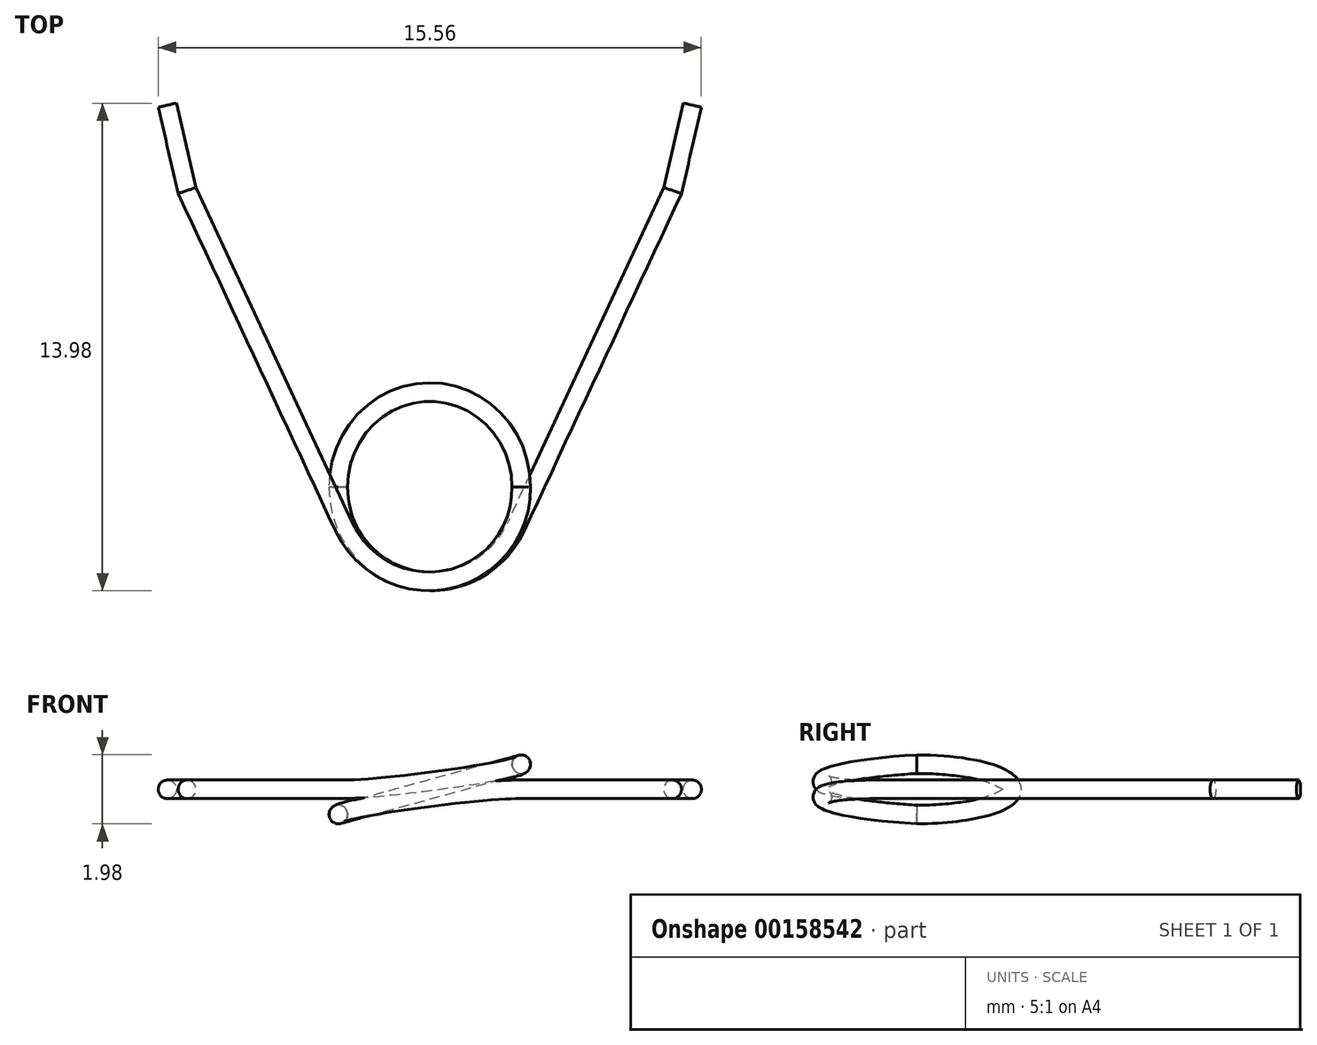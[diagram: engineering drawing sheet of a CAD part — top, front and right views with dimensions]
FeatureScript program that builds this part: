
annotation { "Feature Type Name" : "Feature", "Feature Type Description" : "" }
export const myFeature = defineFeature(function(context is Context, id is Id, definition is map)
    precondition{}
    {
        {
            var Q0;
            Q0=qCreatedBy(makeId("Top.planeOp"),FACE);
            var sketch = newSketch(context, id + "F0", { "sketchPlane" : qUnion([Q0])});
            skCircle(sketch, "E0", {"center": v(0, 0) * mm, "radius": 2.98 * mm, "construction": true});
            skLineSegment(sketch, "E1", {"start": v(2.7, -1.26) * mm, "end": v(7.21, 8.4) * mm});
            skLineSegment(sketch, "E2", {"start": v(7.21, 8.4) * mm, "end": v(7.78, 10.88) * mm});
            skLineSegment(sketch, "E3", {"start": v(-16.33, -2.98) * mm, "end": v(8.7, -2.98) * mm, "construction": true});
            skLineSegment(sketch, "E4", {"start": v(0, 0) * mm, "end": v(0, 10.51) * mm, "construction": true});
            skLineSegment(sketch, "E5", {"start": v(-2.7, -1.26) * mm, "end": v(-7.21, 8.4) * mm, "construction": true});
            skLineSegment(sketch, "E6", {"start": v(-7.21, 8.4) * mm, "end": v(-7.78, 10.88) * mm, "construction": true});
            skSolve(sketch);
        }
        {
            var Q0;
            Q0=sQuery(id+"F0.wireOp",EDGE,"E2");
            var Q1;
            Q1=sQuery(id+"F0.wireOp",VERTEX,"E2.end");
            cPlane(context, id + "F1", {"entities" : qUnion([Q0, Q1]), "cplaneType" : CPlaneType.LINE_POINT, "offset" : 25.4 * mm, "width" : 152.4 * mm, "height" : 152.4 * mm});
        }
        {
            var Q0;
            Q0=qCreatedBy(id+"F1.planeOp",FACE);
            var sketch = newSketch(context, id + "F2", { "sketchPlane" : qUnion([Q0])});
            skCircle(sketch, "E7", {"center": v(-4.87, 0) * mm, "radius": 0.27 * mm});
            skSolve(sketch);
        }
        {
            var Q0;
            Q0=makeQuery(id+"F2.imprint","IMPRINT",FACE,{"disambiguationData":[TD([[makeQuery(id+"F2.imprint","IMPRINT",EDGE,{"derivedFrom":sQuery(id+"F2.wireOp",EDGE,"E7")}),1.0]])]});
            var Q1;
            Q1=sQuery(id+"F0.wireOp",EDGE,"E2");
            var Q2;
            Q2=sQuery(id+"F0.wireOp",EDGE,"E1");
            sweep(context, id + "F3", {"profiles" : qUnion([Q0]), "path" : qUnion([Q1, Q2])});
        }
        {
            var Q0;
            Q0=makeQuery(id+"F3.opSweep","CAP_FACE",FACE,{"disambiguationData":[OSD([sQuery(id+"F0.wireOp",VERTEX,"E1.start"),sQuery(id+"F2.wireOp",EDGE,"E7")])],"isStart":false});
            var sketch = newSketch(context, id + "F4", { "sketchPlane" : qUnion([Q0])});
            skLineSegment(sketch, "E8", {"start": v(0, 0) * mm, "end": v(0.05, -0.38) * mm, "construction": true});
            skLineSegment(sketch, "E9", {"start": v(0.05, -0.38) * mm, "end": v(2.72, 0) * mm, "construction": true});
            skCircle(sketch, "E10.0", {"center": v(2.72, 0) * mm, "radius": 0.27 * mm});
            skSolve(sketch);
        }
        {
            var Q0;
            Q0 = qSketchRegion(id + "F4", true);
            var Q1;
            Q1=sQuery(id+"F4.wireOp",EDGE,"E8");
            revolve(context, id + "F5", {"operationType" : NewBodyOperationType.ADD, "entities" : qUnion([Q0]), "axis" : qUnion([Q1]), "revolveType" : RevolveType.ONE_DIRECTION, "angle" : 270 * degree});
        }
        {
            var Q0;
            Q0=qCreatedBy(makeId("Top.planeOp"),FACE);
            var sketch = newSketch(context, id + "F6", { "sketchPlane" : qUnion([Q0])});
            skLineSegment(sketch, "E11.bottom", {"start": v(-4.83, 4.58) * mm, "end": v(1.68, 4.58) * mm});
            skLineSegment(sketch, "E11.top", {"start": v(-4.83, 0) * mm, "end": v(1.68, 0) * mm});
            skLineSegment(sketch, "E11.left", {"start": v(-4.83, 4.58) * mm, "end": v(-4.83, 0) * mm});
            skLineSegment(sketch, "E11.right", {"start": v(1.68, 4.58) * mm, "end": v(1.68, 0) * mm});
            skSolve(sketch);
        }
        {
            var Q0;
            Q0 = qSketchRegion(id + "F6", true);
            extrude(context, id + "F7", {"entities" : qUnion([Q0]), "operationType" : NewBodyOperationType.REMOVE, "oppositeDirection" : true, "depth" : 25.4 * mm});
        }
        {
            var Q0;
            Q0=makeQuery(id+"F7.boolean.opBoolean","COPY",FACE,{"derivedFrom":makeQuery(id+"F7.opExtrude","SWEPT_FACE",FACE,{"disambiguationData":[OSD([sQuery(id+"F6.wireOp",EDGE,"E11.top")])]})});
            var sketch = newSketch(context, id + "F8", { "sketchPlane" : qUnion([Q0])});
            skLineSegment(sketch, "E12", {"start": v(0, 0) * mm, "end": v(2.62, -0.72) * mm, "construction": true});
            skLineSegment(sketch, "E13", {"start": v(0, 0) * mm, "end": v(0.13, 0.48) * mm, "construction": true});
            skCircle(sketch, "E14", {"center": v(2.62, -0.72) * mm, "radius": 0.27 * mm});
            skSolve(sketch);
        }
        {
            var Q0;
            Q0=makeQuery(id+"F3.opSweep","SWEPT_BODY",BODY,{"disambiguationData":[OSD([sQuery(id+"F0.wireOp",EDGE,"E1"),sQuery(id+"F2.wireOp",EDGE,"E7")])]});
            var Q1;
            Q1=sQuery(id+"F0.wireOp",EDGE,"E4");
            circularPattern(context, id + "F9", {"entities" : qUnion([Q0]), "axis" : qUnion([Q1]), "angle" : 180 * degree, "instanceCount" : 2});
        }
        {
            var Q0;
            Q0 = qSketchRegion(id + "F8", true);
            var Q1;
            Q1=sQuery(id+"F8.wireOp",EDGE,"E13");
            revolve(context, id + "F10", {"entities" : qUnion([Q0]), "axis" : qUnion([Q1]), "revolveType" : RevolveType.ONE_DIRECTION, "oppositeDirection" : true, "angle" : 180 * degree});
        }
    });
